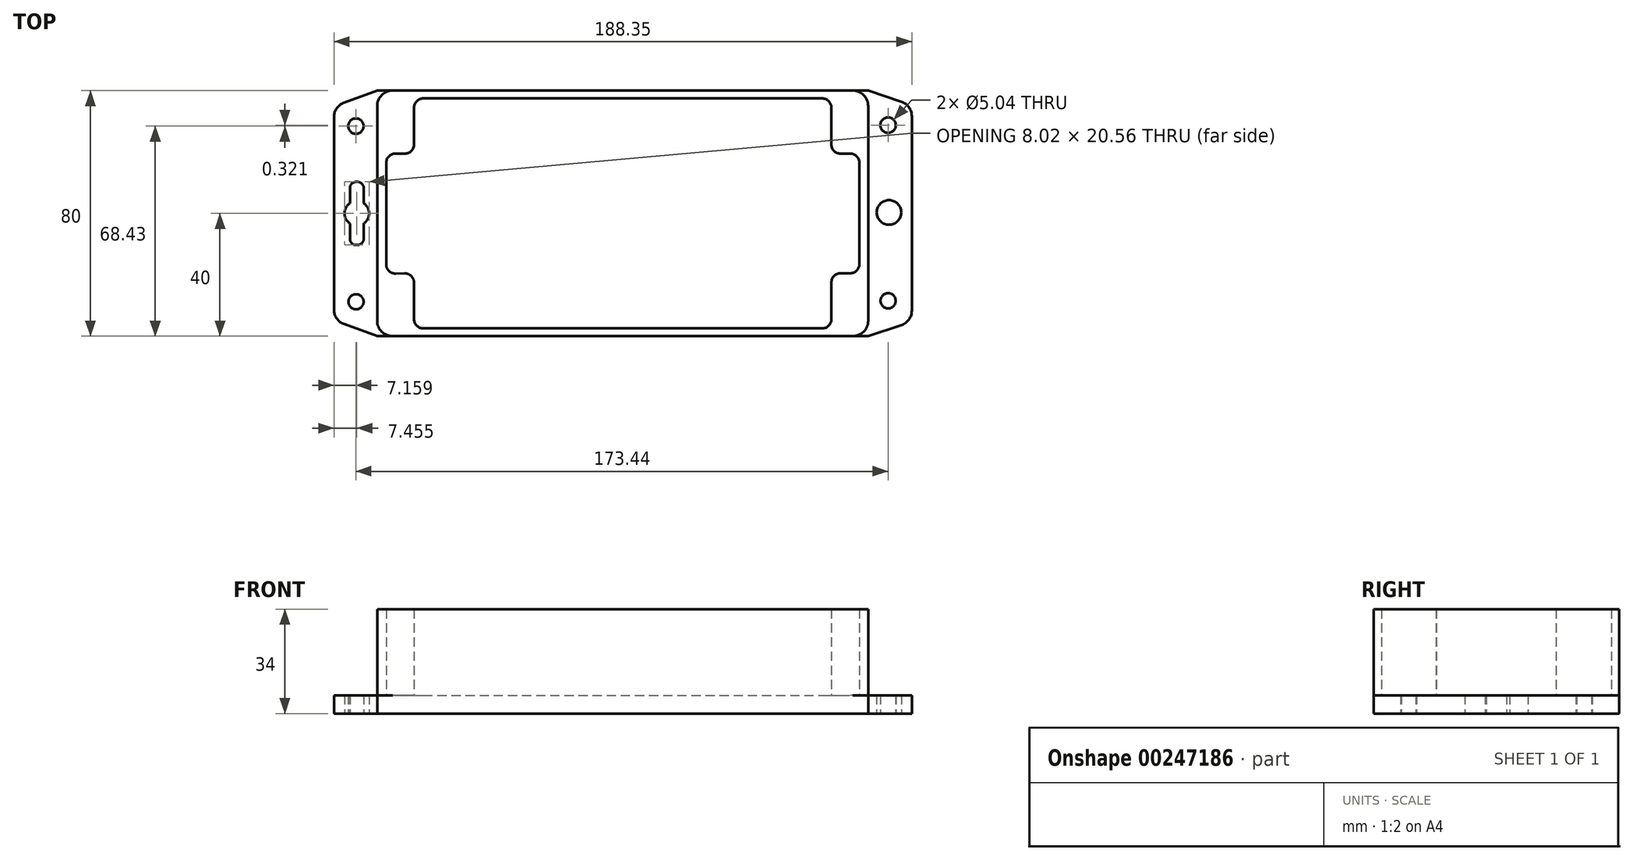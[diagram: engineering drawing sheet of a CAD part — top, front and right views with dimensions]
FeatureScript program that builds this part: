
annotation { "Feature Type Name" : "Feature", "Feature Type Description" : "" }
export const myFeature = defineFeature(function(context is Context, id is Id, definition is map)
    precondition{}
    {
        {
            var Q0;
            Q0=qCreatedBy(makeId("Top.planeOp"),FACE);
            var sketch = newSketch(context, id + "F0", { "sketchPlane" : qUnion([Q0])});
            skLineSegment(sketch, "E0.bottom", {"start": v(75, 40) * mm, "end": v(-75, 40) * mm});
            skLineSegment(sketch, "E0.top", {"start": v(75, -40) * mm, "end": v(-75, -40) * mm});
            skLineSegment(sketch, "E0.left", {"start": v(80, 35) * mm, "end": v(80, -35) * mm});
            skLineSegment(sketch, "E0.right", {"start": v(-80, 35) * mm, "end": v(-80, -35) * mm});
            skPoint(sketch, "E0.middle", {"position": v(0, 0) * mm});
            skLineSegment(sketch, "E1", {"start": v(-80, -40) * mm, "end": v(-90.8, -36.1) * mm});
            skLineSegment(sketch, "E2", {"start": v(-94.1, -31.4) * mm, "end": v(-94.1, 31.4) * mm});
            skLineSegment(sketch, "E3", {"start": v(-90.8, 36.1) * mm, "end": v(-80, 40) * mm});
            skLineSegment(sketch, "E4", {"start": v(80, 40) * mm, "end": v(90.81, 36.41) * mm});
            skLineSegment(sketch, "E5", {"start": v(94.24, 31.67) * mm, "end": v(94.24, -31.67) * mm});
            skLineSegment(sketch, "E6", {"start": v(90.81, -36.41) * mm, "end": v(80, -40) * mm});
            skPoint(sketch, "E7.visualSharp", {"position": v(-94.1, 34.9) * mm});
            skArc(sketch, "E7.filletArc", {"start": v(-90.8, 36.1) * mm, "mid": v(-93.2, 34.26) * mm, "end": v(-94.1, 31.4) * mm});
            skPoint(sketch, "E8.visualSharp", {"position": v(-94.1, -34.9) * mm});
            skArc(sketch, "E8.filletArc", {"start": v(-94.1, -31.4) * mm, "mid": v(-93.2, -34.26) * mm, "end": v(-90.8, -36.1) * mm});
            skPoint(sketch, "E9.visualSharp", {"position": v(94.24, -35.28) * mm});
            skArc(sketch, "E9.filletArc", {"start": v(90.81, -36.41) * mm, "mid": v(93.3, -34.6) * mm, "end": v(94.24, -31.67) * mm});
            skPoint(sketch, "E10.visualSharp", {"position": v(94.24, 35.28) * mm});
            skArc(sketch, "E10.filletArc", {"start": v(94.24, 31.67) * mm, "mid": v(93.3, 34.6) * mm, "end": v(90.81, 36.41) * mm});
            skCircle(sketch, "E11", {"center": v(-86.95, 28.43) * mm, "radius": 2.52 * mm});
            skCircle(sketch, "E12", {"center": v(-86.93, -28.8) * mm, "radius": 2.47 * mm});
            skLineSegment(sketch, "E13.bottom", {"start": v(-86.43, -10.28) * mm, "end": v(-86.88, -10.28) * mm});
            skLineSegment(sketch, "E13.top", {"start": v(-86.43, 10.28) * mm, "end": v(-86.88, 10.28) * mm});
            skLineSegment(sketch, "E13.left", {"start": v(-84.43, -8.28) * mm, "end": v(-84.43, 8.28) * mm});
            skLineSegment(sketch, "E13.right", {"start": v(-88.88, -8.28) * mm, "end": v(-88.88, 8.28) * mm});
            skPoint(sketch, "E13.middle", {"position": v(-86.65, 0) * mm});
            skPoint(sketch, "E14.visualSharp", {"position": v(-88.88, 10.28) * mm});
            skArc(sketch, "E14.filletArc", {"start": v(-86.88, 10.28) * mm, "mid": v(-88.3, 9.7) * mm, "end": v(-88.88, 8.28) * mm});
            skPoint(sketch, "E15.visualSharp", {"position": v(-84.43, 10.28) * mm});
            skArc(sketch, "E15.filletArc", {"start": v(-84.43, 8.28) * mm, "mid": v(-85.01, 9.7) * mm, "end": v(-86.43, 10.28) * mm});
            skPoint(sketch, "E16.visualSharp", {"position": v(-84.43, -10.28) * mm});
            skArc(sketch, "E16.filletArc", {"start": v(-86.43, -10.28) * mm, "mid": v(-85.01, -9.7) * mm, "end": v(-84.43, -8.28) * mm});
            skPoint(sketch, "E17.visualSharp", {"position": v(-88.88, -10.28) * mm});
            skArc(sketch, "E17.filletArc", {"start": v(-88.88, -8.28) * mm, "mid": v(-88.3, -9.7) * mm, "end": v(-86.88, -10.28) * mm});
            skCircle(sketch, "E18", {"center": v(-86.65, 0) * mm, "radius": 4.01 * mm});
            skCircle(sketch, "E19", {"center": v(86.49, 28.75) * mm, "radius": 2.52 * mm});
            skCircle(sketch, "E20", {"center": v(86.51, -28.48) * mm, "radius": 2.47 * mm});
            skLineSegment(sketch, "E21.left", {"start": v(89.01, -7.96) * mm, "end": v(89.01, 8.6) * mm});
            skLineSegment(sketch, "E21.right", {"start": v(84.56, -7.96) * mm, "end": v(84.56, 8.6) * mm});
            skPoint(sketch, "E21.middle", {"position": v(86.79, 0.32) * mm});
            skArc(sketch, "E22.filletArc", {"start": v(86.56, 10.6) * mm, "mid": v(85.14, 10.01) * mm, "end": v(84.56, 8.6) * mm});
            skArc(sketch, "E23.filletArc", {"start": v(89.01, 8.6) * mm, "mid": v(88.43, 10.01) * mm, "end": v(87.01, 10.6) * mm});
            skArc(sketch, "E24.filletArc", {"start": v(87.01, -9.96) * mm, "mid": v(88.43, -9.37) * mm, "end": v(89.01, -7.96) * mm});
            skArc(sketch, "E25.filletArc", {"start": v(84.56, -7.96) * mm, "mid": v(85.14, -9.37) * mm, "end": v(86.56, -9.96) * mm});
            skCircle(sketch, "E26", {"center": v(86.79, 0.32) * mm, "radius": 4.01 * mm});
            skPoint(sketch, "E27.visualSharp", {"position": v(-80, 40) * mm});
            skArc(sketch, "E27.filletArc", {"start": v(-75, 40) * mm, "mid": v(-78.54, 38.54) * mm, "end": v(-80, 35) * mm});
            skPoint(sketch, "E28.visualSharp", {"position": v(-80, -40) * mm});
            skArc(sketch, "E28.filletArc", {"start": v(-80, -35) * mm, "mid": v(-78.54, -38.54) * mm, "end": v(-75, -40) * mm});
            skPoint(sketch, "E29.visualSharp", {"position": v(80, -40) * mm});
            skArc(sketch, "E29.filletArc", {"start": v(75, -40) * mm, "mid": v(78.54, -38.54) * mm, "end": v(80, -35) * mm});
            skPoint(sketch, "E30.visualSharp", {"position": v(80, 40) * mm});
            skArc(sketch, "E30.filletArc", {"start": v(80, 35) * mm, "mid": v(78.54, 38.54) * mm, "end": v(75, 40) * mm});
            skLineSegment(sketch, "E31", {"start": v(-80, 40) * mm, "end": v(-75, 40) * mm});
            skLineSegment(sketch, "E32", {"start": v(-80, -40) * mm, "end": v(-75, -40) * mm});
            skLineSegment(sketch, "E33", {"start": v(75, 40) * mm, "end": v(80, 40) * mm});
            skLineSegment(sketch, "E34", {"start": v(75, -40) * mm, "end": v(80, -40) * mm});
            skLineSegment(sketch, "E35", {"start": v(-65, 37.47) * mm, "end": v(0, 37.47) * mm});
            skLineSegment(sketch, "E36", {"start": v(0, 37.47) * mm, "end": v(65, 37.47) * mm});
            skLineSegment(sketch, "E37", {"start": v(0, -37.49) * mm, "end": v(65, -37.49) * mm});
            skLineSegment(sketch, "E38", {"start": v(0, -37.49) * mm, "end": v(-65, -37.49) * mm});
            skLineSegment(sketch, "E39", {"start": v(-68, 34.47) * mm, "end": v(-68, 22.47) * mm});
            skLineSegment(sketch, "E40", {"start": v(-68, -34.49) * mm, "end": v(-68, -22.55) * mm});
            skLineSegment(sketch, "E41", {"start": v(68, 34.47) * mm, "end": v(68, 22.47) * mm});
            skLineSegment(sketch, "E42", {"start": v(68, -34.49) * mm, "end": v(68, -22.49) * mm});
            skLineSegment(sketch, "E43", {"start": v(-71, 19.47) * mm, "end": v(-74.09, 19.47) * mm});
            skLineSegment(sketch, "E44", {"start": v(-77.09, 16.47) * mm, "end": v(-77.09, -16.6) * mm});
            skLineSegment(sketch, "E45", {"start": v(-74.03, -19.6) * mm, "end": v(-71.06, -19.55) * mm});
            skLineSegment(sketch, "E46", {"start": v(71, 19.47) * mm, "end": v(74.17, 19.47) * mm});
            skLineSegment(sketch, "E47", {"start": v(77.17, 16.47) * mm, "end": v(77.17, -16.49) * mm});
            skLineSegment(sketch, "E48", {"start": v(74.17, -19.49) * mm, "end": v(71, -19.49) * mm});
            skPoint(sketch, "E49.visualSharp", {"position": v(-68, 19.47) * mm});
            skArc(sketch, "E49.filletArc", {"start": v(-71, 19.47) * mm, "mid": v(-68.88, 20.35) * mm, "end": v(-68, 22.47) * mm});
            skPoint(sketch, "E50.visualSharp", {"position": v(-77.09, 19.47) * mm});
            skArc(sketch, "E50.filletArc", {"start": v(-74.09, 19.47) * mm, "mid": v(-76.2, 18.59) * mm, "end": v(-77.09, 16.47) * mm});
            skPoint(sketch, "E51.visualSharp", {"position": v(-77.09, -19.67) * mm});
            skArc(sketch, "E51.filletArc", {"start": v(-77.09, -16.6) * mm, "mid": v(-76.19, -18.75) * mm, "end": v(-74.03, -19.6) * mm});
            skPoint(sketch, "E52.visualSharp", {"position": v(-68, -19.49) * mm});
            skArc(sketch, "E52.filletArc", {"start": v(-68, -22.55) * mm, "mid": v(-68.9, -20.4) * mm, "end": v(-71.06, -19.55) * mm});
            skPoint(sketch, "E53.visualSharp", {"position": v(-68, -37.49) * mm});
            skArc(sketch, "E53.filletArc", {"start": v(-68, -34.49) * mm, "mid": v(-67.12, -36.6) * mm, "end": v(-65, -37.49) * mm});
            skPoint(sketch, "E54.visualSharp", {"position": v(68, -37.49) * mm});
            skArc(sketch, "E54.filletArc", {"start": v(65, -37.49) * mm, "mid": v(67.12, -36.6) * mm, "end": v(68, -34.49) * mm});
            skPoint(sketch, "E55.visualSharp", {"position": v(68, -19.49) * mm});
            skArc(sketch, "E55.filletArc", {"start": v(71, -19.49) * mm, "mid": v(68.88, -20.36) * mm, "end": v(68, -22.49) * mm});
            skPoint(sketch, "E56.visualSharp", {"position": v(77.17, -19.49) * mm});
            skArc(sketch, "E56.filletArc", {"start": v(74.17, -19.49) * mm, "mid": v(76.3, -18.6) * mm, "end": v(77.17, -16.49) * mm});
            skPoint(sketch, "E57.visualSharp", {"position": v(77.17, 19.47) * mm});
            skArc(sketch, "E57.filletArc", {"start": v(77.17, 16.47) * mm, "mid": v(76.3, 18.59) * mm, "end": v(74.17, 19.47) * mm});
            skPoint(sketch, "E58.visualSharp", {"position": v(68, 19.47) * mm});
            skArc(sketch, "E58.filletArc", {"start": v(68, 22.47) * mm, "mid": v(68.88, 20.35) * mm, "end": v(71, 19.47) * mm});
            skPoint(sketch, "E59.visualSharp", {"position": v(68, 37.47) * mm});
            skArc(sketch, "E59.filletArc", {"start": v(68, 34.47) * mm, "mid": v(67.12, 36.59) * mm, "end": v(65, 37.47) * mm});
            skPoint(sketch, "E60.visualSharp", {"position": v(-68, 37.47) * mm});
            skArc(sketch, "E60.filletArc", {"start": v(-65, 37.47) * mm, "mid": v(-67.12, 36.59) * mm, "end": v(-68, 34.47) * mm});
            skSolve(sketch);
        }
        {
            var Q0;
            Q0=makeQuery(id+"F0.imprint","IMPRINT",FACE,{"disambiguationData":[TD([[makeQuery(id+"F0.imprint","IMPRINT",EDGE,{"derivedFrom":sQuery(id+"F0.wireOp",EDGE,"E0.bottom")}),1.0]])]});
            var Q1;
            Q1=makeQuery(id+"F0.imprint","IMPRINT",FACE,{"disambiguationData":[TD([[makeQuery(id+"F0.imprint","IMPRINT",EDGE,{"derivedFrom":sQuery(id+"F0.wireOp",EDGE,"E0.left")}),1.0]])]});
            var Q2;
            Q2=makeQuery(id+"F0.imprint","IMPRINT",FACE,{"disambiguationData":[TD([[makeQuery(id+"F0.imprint","IMPRINT",EDGE,{"derivedFrom":sQuery(id+"F0.wireOp",EDGE,"E0.right")}),-1.0]])]});
            extrude(context, id + "F1", {"entities" : qUnion([Q0, Q1, Q2]), "depth" : 6 * mm});
        }
        {
            var Q0;
            Q0=makeQuery(id+"F0.imprint","IMPRINT",FACE,{"disambiguationData":[TD([[makeQuery(id+"F0.imprint","IMPRINT",EDGE,{"derivedFrom":sQuery(id+"F0.wireOp",EDGE,"E0.bottom")}),1.0]])]});
            extrude(context, id + "F2", {"entities" : qUnion([Q0]), "operationType" : NewBodyOperationType.ADD, "depth" : 34 * mm});
        }
        {
            var Q0;
            Q0=makeQuery(id+"F0.imprint","IMPRINT",FACE,{"disambiguationData":[TD([[makeQuery(id+"F0.imprint","IMPRINT",EDGE,{"derivedFrom":sQuery(id+"F0.wireOp",EDGE,"E35")}),-1.0]])]});
            var Q1;
            Q1=makeQuery(id+"F0.imprint","IMPRINT",FACE,{"disambiguationData":[TD([[makeQuery(id+"F0.imprint","IMPRINT",EDGE,{"derivedFrom":sQuery(id+"F0.wireOp",EDGE,"E0.bottom")}),1.0]])]});
            var Q2;
            Q2=makeQuery(id+"F0.imprint","IMPRINT",FACE,{"disambiguationData":[TD([[makeQuery(id+"F0.imprint","IMPRINT",EDGE,{"derivedFrom":sQuery(id+"F0.wireOp",EDGE,"E0.right")}),-1.0]])]});
            var Q3;
            Q3=makeQuery(id+"F0.imprint","IMPRINT",FACE,{"disambiguationData":[TD([[makeQuery(id+"F0.imprint","IMPRINT",EDGE,{"derivedFrom":sQuery(id+"F0.wireOp",EDGE,"E0.left")}),1.0]])]});
            extrude(context, id + "F3", {"entities" : qUnion([Q0, Q1, Q2, Q3]), "operationType" : NewBodyOperationType.ADD, "depth" : 6 * mm});
        }
    });
